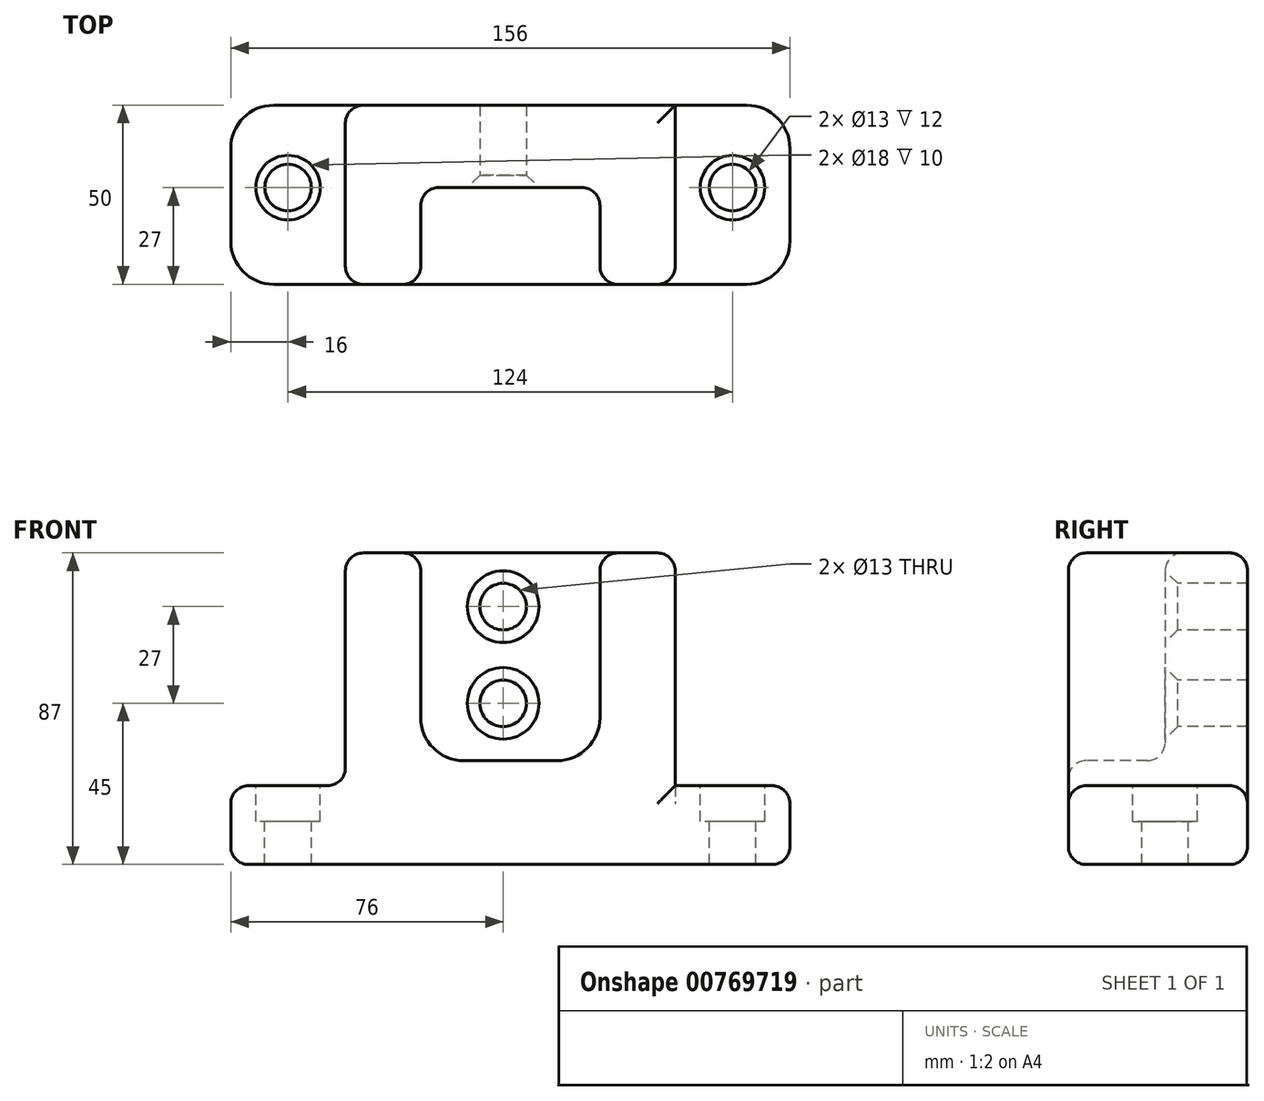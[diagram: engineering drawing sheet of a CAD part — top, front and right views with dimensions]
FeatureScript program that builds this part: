
annotation { "Feature Type Name" : "Feature", "Feature Type Description" : "" }
export const myFeature = defineFeature(function(context is Context, id is Id, definition is map)
    precondition{}
    {
        {
            var Q0;
            Q0=qCreatedBy(makeId("Top.planeOp"),FACE);
            var sketch = newSketch(context, id + "F0", { "sketchPlane" : qUnion([Q0])});
            skLineSegment(sketch, "E0.bottom", {"start": v(0, 0) * mm, "end": v(156, 0) * mm});
            skLineSegment(sketch, "E0.top", {"start": v(0, 50) * mm, "end": v(156, 50) * mm});
            skLineSegment(sketch, "E0.left", {"start": v(0, 0) * mm, "end": v(0, 50) * mm});
            skLineSegment(sketch, "E0.right", {"start": v(156, 0) * mm, "end": v(156, 50) * mm});
            skSolve(sketch);
        }
        {
            var Q0;
            Q0 = qSketchRegion(id + "F0", true);
            extrude(context, id + "F1", {"entities" : qUnion([Q0]), "depth" : 87 * mm, "offsetDistance" : 25 * mm});
        }
        {
            var Q0;
            Q0=makeQuery(id+"F1.opExtrude","SWEPT_FACE",FACE,{"disambiguationData":[OSD([sQuery(id+"F0.wireOp",EDGE,"E0.bottom")])]});
            var sketch = newSketch(context, id + "F2", { "sketchPlane" : qUnion([Q0])});
            skLineSegment(sketch, "E1.bottom", {"start": v(0, 87) * mm, "end": v(32, 87) * mm});
            skLineSegment(sketch, "E1.top", {"start": v(0, 22) * mm, "end": v(32, 22) * mm});
            skLineSegment(sketch, "E1.left", {"start": v(0, 87) * mm, "end": v(0, 22) * mm});
            skLineSegment(sketch, "E1.right", {"start": v(32, 87) * mm, "end": v(32, 22) * mm});
            skLineSegment(sketch, "E2.bottom", {"start": v(156, 87) * mm, "end": v(124, 87) * mm});
            skLineSegment(sketch, "E2.top", {"start": v(156, 22) * mm, "end": v(124, 22) * mm});
            skLineSegment(sketch, "E2.left", {"start": v(156, 87) * mm, "end": v(156, 22) * mm});
            skLineSegment(sketch, "E2.right", {"start": v(124, 87) * mm, "end": v(124, 22) * mm});
            skSolve(sketch);
        }
        {
            var Q0;
            Q0 = qSketchRegion(id + "F2", true);
            extrude(context, id + "F3", {"entities" : qUnion([Q0]), "operationType" : NewBodyOperationType.REMOVE, "endBound" : BoundingType.UP_TO_NEXT, "oppositeDirection" : true, "depth" : 25 * mm, "offsetDistance" : 25 * mm});
        }
        {
            var Q0;
            Q0=makeQuery(id+"F1.opExtrude","SWEPT_FACE",FACE,{"disambiguationData":[OSD([sQuery(id+"F0.wireOp",EDGE,"E0.bottom")])]});
            var sketch = newSketch(context, id + "F4", { "sketchPlane" : qUnion([Q0])});
            skLineSegment(sketch, "E3.bottom", {"start": v(53, 87) * mm, "end": v(103, 87) * mm});
            skLineSegment(sketch, "E3.top", {"start": v(53, 29) * mm, "end": v(103, 29) * mm});
            skLineSegment(sketch, "E3.left", {"start": v(53, 87) * mm, "end": v(53, 29) * mm});
            skLineSegment(sketch, "E3.right", {"start": v(103, 87) * mm, "end": v(103, 29) * mm});
            skSolve(sketch);
        }
        {
            var Q0;
            Q0 = qSketchRegion(id + "F4", true);
            extrude(context, id + "F5", {"entities" : qUnion([Q0]), "operationType" : NewBodyOperationType.REMOVE, "oppositeDirection" : true, "depth" : 27 * mm, "offsetDistance" : 25 * mm});
        }
        {
            var Q0;
            Q0=makeQuery(id+"F3.boolean.opBoolean","COPY",FACE,{"derivedFrom":makeQuery(id+"F3.opExtrude","SWEPT_FACE",FACE,{"disambiguationData":[OSD([sQuery(id+"F2.wireOp",EDGE,"E2.top")])]})});
            var sketch = newSketch(context, id + "F6", { "sketchPlane" : qUnion([Q0])});
            skPoint(sketch, "E4", {"position": v(140, 27) * mm});
            skPoint(sketch, "E5", {"position": v(16, 27) * mm});
            skSolve(sketch);
        }
        {
            var Q0;
            Q0=sQuery(id+"F6.wireOp",VERTEX,"E5");
            var Q1;
            Q1=sQuery(id+"F6.wireOp",VERTEX,"E4");
            var Q2;
            Q2=makeQuery(id+"F1.opExtrude","SWEPT_BODY",BODY,{"disambiguationData":[OSD([sQuery(id+"F0.wireOp",EDGE,"E0.bottom"),sQuery(id+"F0.wireOp",EDGE,"E0.top"),sQuery(id+"F0.wireOp",EDGE,"E0.left"),sQuery(id+"F0.wireOp",EDGE,"E0.right")])]});
            hole(context, id + "F7", {"style" : HoleStyle.C_BORE, "endStyle" : HoleEndStyle.THROUGH, "holeDiameter" : 13 * mm, "cBoreDiameter" : 18 * mm, "cBoreDepth" : 10 * mm, "majorDiameter" : 5 * mm, "isTappedThrough" : true, "tappedDepth" : 12 * mm, "tapClearance" : 3, "locations" : qUnion([Q0, Q1]), "scope" : qUnion([Q2])});
        }
        {
            var Q0;
            Q0=makeQuery(id+"F5.boolean.opBoolean","COPY",FACE,{"derivedFrom":makeQuery(id+"F5.opExtrude","CAP_FACE",FACE,{"disambiguationData":[OSD([sQuery(id+"F4.wireOp",EDGE,"E3.bottom"),sQuery(id+"F4.wireOp",EDGE,"E3.top"),sQuery(id+"F4.wireOp",EDGE,"E3.left"),sQuery(id+"F4.wireOp",EDGE,"E3.right")])],"isStart":false})});
            var sketch = newSketch(context, id + "F8", { "sketchPlane" : qUnion([Q0])});
            skPoint(sketch, "E6", {"position": v(76, 72) * mm});
            skPoint(sketch, "E7", {"position": v(76, 45) * mm});
            skSolve(sketch);
        }
        {
            var Q0;
            Q0=sQuery(id+"F8.wireOp",VERTEX,"E6");
            var Q1;
            Q1=sQuery(id+"F8.wireOp",VERTEX,"E7");
            var Q2;
            Q2=makeQuery(id+"F1.opExtrude","SWEPT_BODY",BODY,{"disambiguationData":[OSD([sQuery(id+"F0.wireOp",EDGE,"E0.bottom"),sQuery(id+"F0.wireOp",EDGE,"E0.top"),sQuery(id+"F0.wireOp",EDGE,"E0.left"),sQuery(id+"F0.wireOp",EDGE,"E0.right")])]});
            hole(context, id + "F9", {"style" : HoleStyle.C_SINK, "endStyle" : HoleEndStyle.THROUGH, "holeDiameter" : 13 * mm, "cSinkDiameter" : 20 * mm, "cSinkAngle" : 90 * degree, "majorDiameter" : 5 * mm, "isTappedThrough" : true, "tappedDepth" : 12 * mm, "tapClearance" : 3, "locations" : qUnion([Q0, Q1]), "scope" : qUnion([Q2])});
        }
        {
            var Q0;
            Q0=makeQuery(id+"F5.boolean.opBoolean","COPY",EDGE,{"derivedFrom":makeQuery(id+"F5.opExtrude","SWEPT_EDGE",EDGE,{"disambiguationData":[OSD([sQuery(id+"F4.wireOp",EDGE,"E3.top"),sQuery(id+"F4.wireOp",EDGE,"E3.left")])]})});
            var Q1;
            Q1=makeQuery(id+"F5.boolean.opBoolean","COPY",EDGE,{"derivedFrom":makeQuery(id+"F5.opExtrude","SWEPT_EDGE",EDGE,{"disambiguationData":[OSD([sQuery(id+"F4.wireOp",EDGE,"E3.top"),sQuery(id+"F4.wireOp",EDGE,"E3.right")])]})});
            var Q2;
            Q2=makeQuery(id+"F1.opExtrude","SWEPT_EDGE",EDGE,{"disambiguationData":[OSD([sQuery(id+"F0.wireOp",EDGE,"E0.bottom"),sQuery(id+"F0.wireOp",EDGE,"E0.left")])]});
            var Q3;
            Q3=makeQuery(id+"F1.opExtrude","SWEPT_EDGE",EDGE,{"disambiguationData":[OSD([sQuery(id+"F0.wireOp",EDGE,"E0.top"),sQuery(id+"F0.wireOp",EDGE,"E0.left")])]});
            var Q4;
            Q4=makeQuery(id+"F1.opExtrude","SWEPT_EDGE",EDGE,{"disambiguationData":[OSD([sQuery(id+"F0.wireOp",EDGE,"E0.top"),sQuery(id+"F0.wireOp",EDGE,"E0.right")])]});
            var Q5;
            Q5=makeQuery(id+"F1.opExtrude","SWEPT_EDGE",EDGE,{"disambiguationData":[OSD([sQuery(id+"F0.wireOp",EDGE,"E0.bottom"),sQuery(id+"F0.wireOp",EDGE,"E0.right")])]});
            fillet(context, id + "F10", {"entities" : qUnion([Q0, Q1, Q2, Q3, Q4, Q5]), "radius" : 12 * mm, "tangentPropagation" : true, "allowEdgeOverflow" : false});
        }
        {
            var Q0;
            Q0=makeQuery(id+"F1.opExtrude","CAP_FACE",FACE,{"disambiguationData":[OSD([sQuery(id+"F0.wireOp",EDGE,"E0.bottom"),sQuery(id+"F0.wireOp",EDGE,"E0.top"),sQuery(id+"F0.wireOp",EDGE,"E0.left"),sQuery(id+"F0.wireOp",EDGE,"E0.right")])],"isStart":false});
            var Q1;
            Q1=makeQuery(id+"F1.opExtrude","SWEPT_FACE",FACE,{"disambiguationData":[OSD([sQuery(id+"F0.wireOp",EDGE,"E0.bottom")])]});
            var Q2;
            Q2=makeQuery(id+"F5.boolean.opBoolean","COPY",FACE,{"derivedFrom":makeQuery(id+"F5.opExtrude","SWEPT_FACE",FACE,{"disambiguationData":[OSD([sQuery(id+"F4.wireOp",EDGE,"E3.left")])]})});
            var Q3;
            Q3=makeQuery(id+"F10.opFillet","BLEND_FACE",FACE,{"disambiguationData":[OSD([sQuery(id+"F4.wireOp",EDGE,"E3.top"),sQuery(id+"F4.wireOp",EDGE,"E3.left")])]});
            var Q4;
            Q4=makeQuery(id+"F5.boolean.opBoolean","COPY",FACE,{"derivedFrom":makeQuery(id+"F5.opExtrude","SWEPT_FACE",FACE,{"disambiguationData":[OSD([sQuery(id+"F4.wireOp",EDGE,"E3.top")])]})});
            var Q5;
            Q5=makeQuery(id+"F10.opFillet","BLEND_FACE",FACE,{"disambiguationData":[OSD([sQuery(id+"F4.wireOp",EDGE,"E3.top"),sQuery(id+"F4.wireOp",EDGE,"E3.right")])]});
            var Q6;
            Q6=makeQuery(id+"F5.boolean.opBoolean","COPY",FACE,{"derivedFrom":makeQuery(id+"F5.opExtrude","SWEPT_FACE",FACE,{"disambiguationData":[OSD([sQuery(id+"F4.wireOp",EDGE,"E3.right")])]})});
            var Q7;
            Q7=makeQuery(id+"F3.boolean.opBoolean","COPY",FACE,{"derivedFrom":makeQuery(id+"F3.opExtrude","SWEPT_FACE",FACE,{"disambiguationData":[OSD([sQuery(id+"F2.wireOp",EDGE,"E1.right")])]})});
            fillet(context, id + "F11", {"entities" : qUnion([Q0, Q1, Q2, Q3, Q4, Q5, Q6, Q7]), "radius" : 5 * mm, "tangentPropagation" : true, "allowEdgeOverflow" : false});
        }
    });
